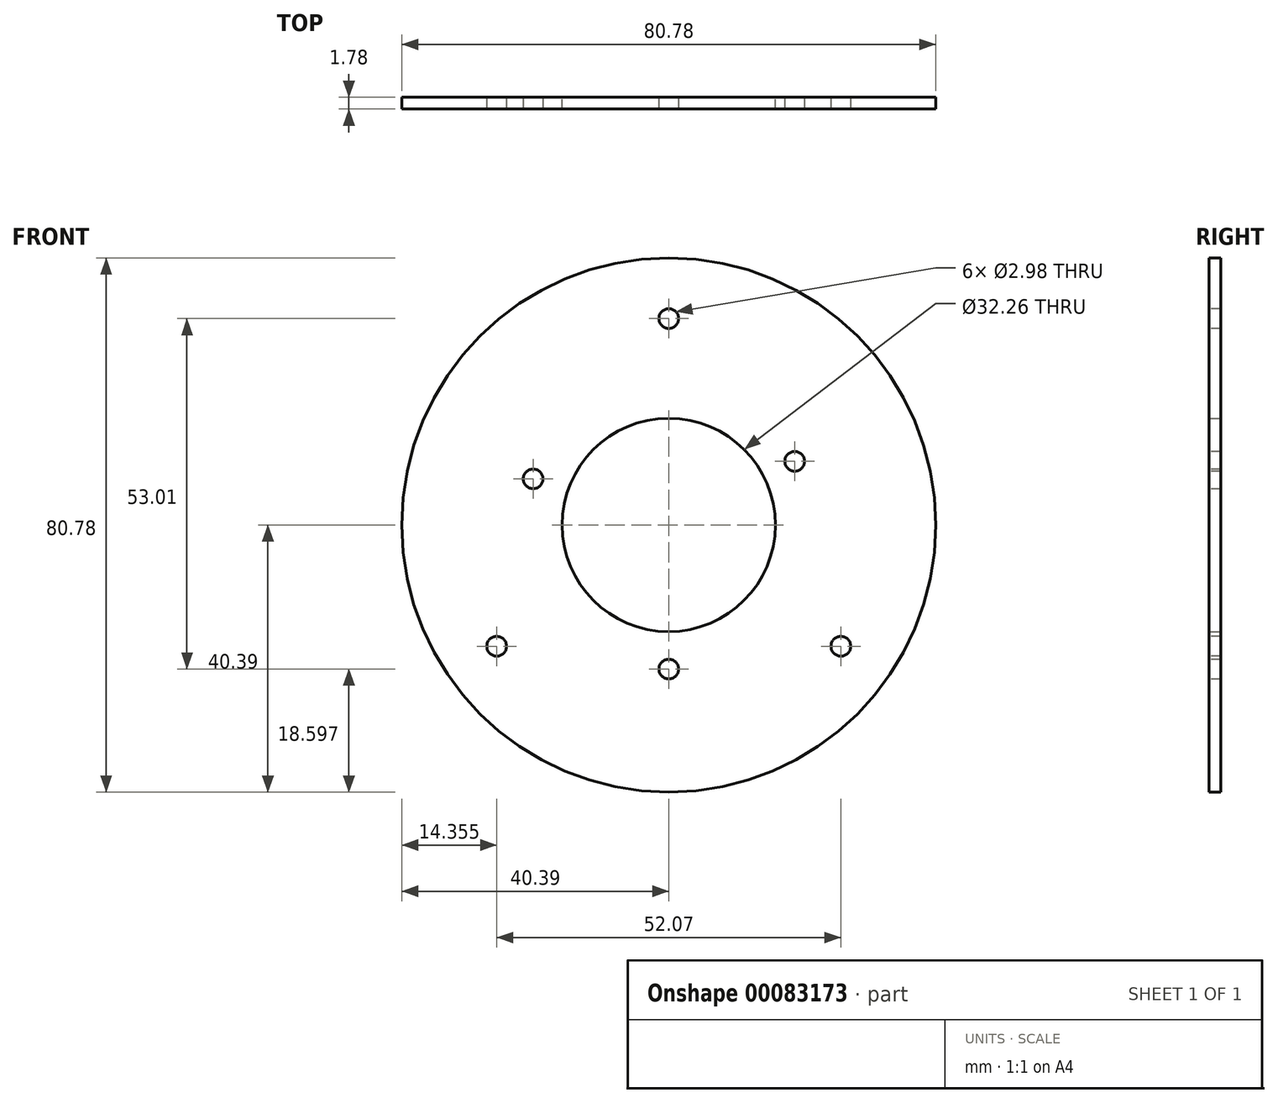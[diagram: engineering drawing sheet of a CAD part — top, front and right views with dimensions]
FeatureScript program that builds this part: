
annotation { "Feature Type Name" : "Feature", "Feature Type Description" : "" }
export const myFeature = defineFeature(function(context is Context, id is Id, definition is map)
    precondition{}
    {
        {
            var Q0;
            Q0=qCreatedBy(makeId("Front.planeOp"),FACE);
            var sketch = newSketch(context, id + "F0", { "sketchPlane" : qUnion([Q0])});
            skCircle(sketch, "E0", {"center": v(0, 0) * mm, "radius": 40.39 * mm});
            skCircle(sketch, "E1", {"center": v(0, 0) * mm, "radius": 16.13 * mm});
            skSolve(sketch);
        }
        {
            var Q0;
            Q0=makeQuery(id+"F0.imprint","IMPRINT",FACE,{"disambiguationData":[TD([[makeQuery(id+"F0.imprint","IMPRINT",EDGE,{"derivedFrom":sQuery(id+"F0.wireOp",EDGE,"E0")}),1.0]])]});
            extrude(context, id + "F1", {"entities" : qUnion([Q0]), "depth" : 1.78 * mm});
        }
        {
            var Q0;
            Q0=makeQuery(id+"F1.opExtrude","CAP_FACE",FACE,{"disambiguationData":[OSD([sQuery(id+"F0.wireOp",EDGE,"E0"),sQuery(id+"F0.wireOp",EDGE,"E1")])],"isStart":false});
            var sketch = newSketch(context, id + "F2", { "sketchPlane" : qUnion([Q0])});
            skLineSegment(sketch, "E2", {"start": v(0, 58.93) * mm, "end": v(0, -65.67) * mm, "construction": true});
            skLineSegment(sketch, "E3", {"start": v(78.08, 0) * mm, "end": v(-88.23, 0) * mm, "construction": true});
            skPoint(sketch, "E4", {"position": v(0, 31.22) * mm});
            skPoint(sketch, "E5", {"position": v(0, -21.8) * mm});
            skPoint(sketch, "E6", {"position": v(26.04, -18.34) * mm});
            skPoint(sketch, "E7", {"position": v(-26.03, -18.34) * mm});
            skPoint(sketch, "E8", {"position": v(-20.52, 6.97) * mm});
            skPoint(sketch, "E9", {"position": v(19.05, 9.63) * mm});
            skSolve(sketch);
        }
        {
            var Q0;
            Q0=sQuery(id+"F2.wireOp",VERTEX,"E4");
            var Q1;
            Q1=sQuery(id+"F2.wireOp",VERTEX,"E9");
            var Q2;
            Q2=sQuery(id+"F2.wireOp",VERTEX,"E6");
            var Q3;
            Q3=sQuery(id+"F2.wireOp",VERTEX,"E5");
            var Q4;
            Q4=sQuery(id+"F2.wireOp",VERTEX,"E7");
            var Q5;
            Q5=sQuery(id+"F2.wireOp",VERTEX,"E8");
            var Q6;
            Q6=makeQuery(id+"F1.opExtrude","SWEPT_BODY",BODY,{"disambiguationData":[OSD([sQuery(id+"F0.wireOp",EDGE,"E0"),sQuery(id+"F0.wireOp",EDGE,"E1")])]});
            hole(context, id + "F3", {"style" : HoleStyle.SIMPLE, "endStyle" : HoleEndStyle.THROUGH, "holeDiameter" : 2.98 * mm, "locations" : qUnion([Q0, Q1, Q2, Q3, Q4, Q5]), "scope" : qUnion([Q6]), "isTappedThrough" : true});
        }
    });
